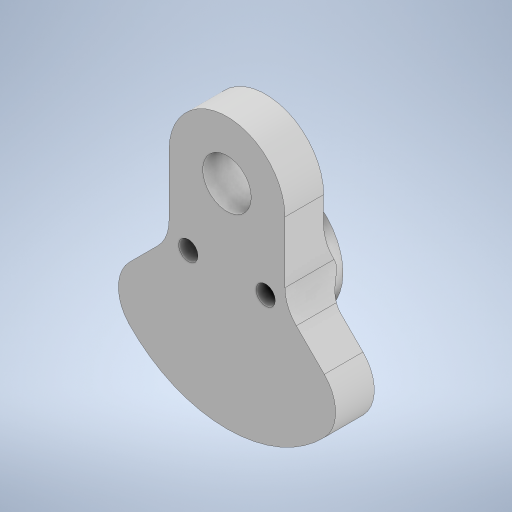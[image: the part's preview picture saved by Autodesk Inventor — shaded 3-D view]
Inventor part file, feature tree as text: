
AUTODESK INVENTOR PART (.ipt)
format: ipt  version: 2023 (Build 270158000, 158)  size: 293,888 bytes
history: native  units: in
note: dims shown in document units (in); Inventor stores cm internally (conversion verified against a paired STEP export)
features: extrude x2, sketch x1, fillet x1
ambient origin geometry x8: Origin, YZ Plane, XZ Plane, XY Plane, X Axis, Y Axis, Z Axis, Center Point
bodies: Body1 (feature_tree)
feature tree (4):
  sketch  "Sketch1"  dims[d3=0.866in d15=0.75in d20=0.314in d31=0.25in d32=0.0in d34=1.75in d35=0.25in d36=0.25in d37=0.75in d38=0.5in d39=0.125in d40=0.0in d41=0.125in]
  extrude  "Extrusion2"  Depth=0.125in
  extrude  "Extrusion3"  Depth=0.25in TaperAngle=0.0deg
  fillet  "Fillet1"  Radius=1.75in
